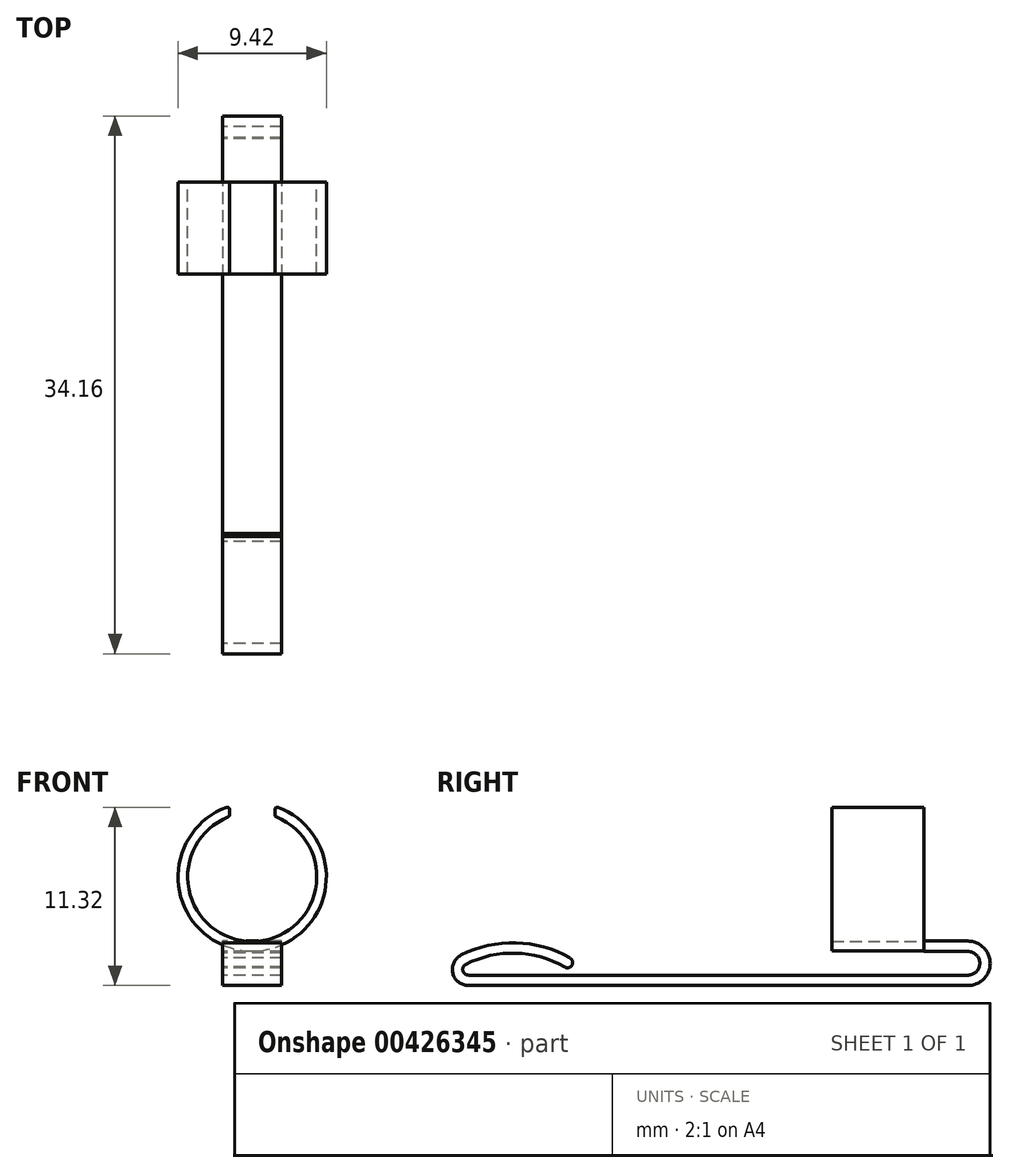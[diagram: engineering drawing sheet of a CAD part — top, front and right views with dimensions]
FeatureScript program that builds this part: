
annotation { "Feature Type Name" : "Feature", "Feature Type Description" : "" }
export const myFeature = defineFeature(function(context is Context, id is Id, definition is map)
    precondition{}
    {
        {
            var Q0;
            Q0=qCreatedBy(makeId("Front.planeOp"),FACE);
            var sketch = newSketch(context, id + "F0", { "sketchPlane" : qUnion([Q0])});
            skArc(sketch, "E0", {"start": v(-1.53, 3.8) * mm, "mid": v(0, -4.1) * mm, "end": v(1.53, 3.8) * mm});
            skArc(sketch, "E1", {"start": v(-1.64, 4.41) * mm, "mid": v(0, -4.71) * mm, "end": v(1.64, 4.41) * mm});
            skLineSegment(sketch, "E2", {"start": v(-1.44, 4.27) * mm, "end": v(-1.44, 3.94) * mm});
            skLineSegment(sketch, "E3", {"start": v(1.44, 4.27) * mm, "end": v(1.44, 3.94) * mm});
            skPoint(sketch, "E4.visualSharp", {"position": v(-1.44, 4.48) * mm});
            skArc(sketch, "E4.filletArc", {"start": v(-1.44, 4.27) * mm, "mid": v(-1.5, 4.4) * mm, "end": v(-1.64, 4.41) * mm});
            skPoint(sketch, "E5.visualSharp", {"position": v(-1.44, 3.84) * mm});
            skArc(sketch, "E5.filletArc", {"start": v(-1.53, 3.8) * mm, "mid": v(-1.47, 3.86) * mm, "end": v(-1.44, 3.94) * mm});
            skPoint(sketch, "E6.visualSharp", {"position": v(1.44, 3.84) * mm});
            skArc(sketch, "E6.filletArc", {"start": v(1.44, 3.94) * mm, "mid": v(1.47, 3.86) * mm, "end": v(1.53, 3.8) * mm});
            skPoint(sketch, "E7.visualSharp", {"position": v(1.44, 4.48) * mm});
            skArc(sketch, "E7.filletArc", {"start": v(1.64, 4.41) * mm, "mid": v(1.5, 4.4) * mm, "end": v(1.44, 4.27) * mm});
            skSolve(sketch);
        }
        {
            var Q0;
            Q0=qSketchRegion(id+"F0",true);
            extrude(context, id + "F1", {"entities" : qUnion([Q0]), "depth" : 5.84 * mm});
        }
        {
            var Q0;
            Q0=qCreatedBy(makeId("Right.planeOp"),FACE);
            var sketch = newSketch(context, id + "F2", { "sketchPlane" : qUnion([Q0])});
            skLineSegment(sketch, "E8.bottom", {"start": v(0, -4.74) * mm, "end": v(2.8, -4.74) * mm});
            skLineSegment(sketch, "E8.top", {"start": v(0, -4.08) * mm, "end": v(2.79, -4.08) * mm});
            skLineSegment(sketch, "E8.left", {"start": v(0, -4.74) * mm, "end": v(0, -4.08) * mm});
            skLineSegment(sketch, "E8.right", {"start": v(2.8, -4.74) * mm, "end": v(2.8, -4.08) * mm});
            skArc(sketch, "E9", {"start": v(2.8, -4.74) * mm, "mid": v(3.54, -5.5) * mm, "end": v(2.77, -6.24) * mm});
            skLineSegment(sketch, "E10", {"start": v(2.81, -6.24) * mm, "end": v(-28.94, -6.24) * mm});
            skArc(sketch, "E11.0", {"start": v(2.8, -4.08) * mm, "mid": v(4.2, -5.51) * mm, "end": v(2.75, -6.9) * mm});
            skArc(sketch, "E12", {"start": v(-28.94, -6.24) * mm, "mid": v(-29.29, -5.96) * mm, "end": v(-29.1, -5.56) * mm});
            skArc(sketch, "E13", {"start": v(-29.1, -5.56) * mm, "mid": v(-25.94, -4.84) * mm, "end": v(-22.83, -5.73) * mm});
            skArc(sketch, "E14.0", {"start": v(-29.4, -4.97) * mm, "mid": v(-25.93, -4.18) * mm, "end": v(-22.5, -5.15) * mm});
            skArc(sketch, "E14.1", {"start": v(-28.94, -6.9) * mm, "mid": v(-29.93, -6.12) * mm, "end": v(-29.4, -4.97) * mm});
            skLineSegment(sketch, "E14.2", {"start": v(2.81, -6.9) * mm, "end": v(-28.94, -6.9) * mm});
            skArc(sketch, "E15", {"start": v(-22.83, -5.73) * mm, "mid": v(-22.36, -5.61) * mm, "end": v(-22.5, -5.15) * mm});
            skSolve(sketch);
        }
        {
            var Q0;
            Q0=qSketchRegion(id+"F2",true);
            extrude(context, id + "F3", {"entities" : qUnion([Q0]), "operationType" : NewBodyOperationType.ADD, "depth" : 3.75 * mm, "symmetric" : true});
        }
    });
